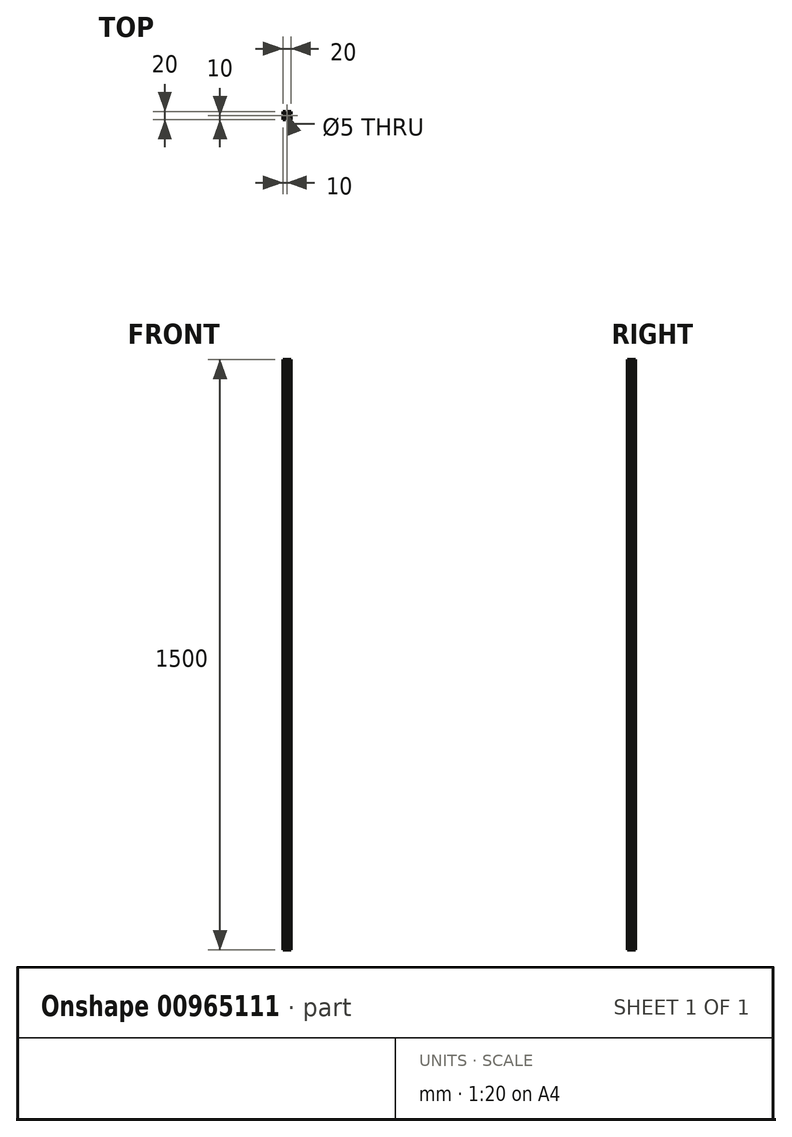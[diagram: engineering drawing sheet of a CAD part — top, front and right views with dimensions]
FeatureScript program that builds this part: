
annotation { "Feature Type Name" : "Feature", "Feature Type Description" : "" }
export const myFeature = defineFeature(function(context is Context, id is Id, definition is map)
    precondition{}
    {
        {
            var Q0;
            Q0=qCreatedBy(makeId("Top.planeOp"),FACE);
            var sketch = newSketch(context, id + "F0", { "sketchPlane" : qUnion([Q0])});
            skCircle(sketch, "E0", {"center": v(10, 10) * mm, "radius": 2.5 * mm});
            skLineSegment(sketch, "E1", {"start": v(0, 0) * mm, "end": v(10, 10) * mm, "construction": true});
            skLineSegment(sketch, "E2", {"start": v(1.4, 2.39) * mm, "end": v(1.4, 6.8) * mm});
            skLineSegment(sketch, "E3", {"start": v(1.4, 6.8) * mm, "end": v(0, 6.8) * mm});
            skLineSegment(sketch, "E4", {"start": v(0, 6.8) * mm, "end": v(0, 0) * mm});
            skLineSegment(sketch, "E5", {"start": v(7.49, 6.5) * mm, "end": v(2.39, 1.4) * mm});
            skLineSegment(sketch, "E6", {"start": v(2.39, 1.4) * mm, "end": v(6.8, 1.4) * mm});
            skLineSegment(sketch, "E7", {"start": v(6.8, 1.4) * mm, "end": v(6.8, 0) * mm});
            skLineSegment(sketch, "E8", {"start": v(6.8, 0) * mm, "end": v(0, 0) * mm});
            skLineSegment(sketch, "E9", {"start": v(10, 10) * mm, "end": v(20, 20) * mm, "construction": true});
            skLineSegment(sketch, "E10", {"start": v(10, 10) * mm, "end": v(0, 20) * mm, "construction": true});
            skLineSegment(sketch, "E11", {"start": v(10, 10) * mm, "end": v(20, 0) * mm, "construction": true});
            skLineSegment(sketch, "E12", {"start": v(1.4, 17.61) * mm, "end": v(6.5, 12.51) * mm});
            skLineSegment(sketch, "E13", {"start": v(1.4, 17.61) * mm, "end": v(1.4, 13.2) * mm});
            skLineSegment(sketch, "E14", {"start": v(1.4, 13.2) * mm, "end": v(0, 13.2) * mm});
            skLineSegment(sketch, "E15", {"start": v(0, 13.2) * mm, "end": v(0, 20) * mm});
            skLineSegment(sketch, "E16", {"start": v(7.49, 13.5) * mm, "end": v(2.39, 18.6) * mm});
            skLineSegment(sketch, "E17", {"start": v(2.39, 18.6) * mm, "end": v(6.8, 18.6) * mm});
            skLineSegment(sketch, "E18", {"start": v(6.8, 18.6) * mm, "end": v(6.8, 20) * mm});
            skLineSegment(sketch, "E19", {"start": v(6.8, 20) * mm, "end": v(0, 20) * mm});
            skLineSegment(sketch, "E20", {"start": v(12.51, 13.5) * mm, "end": v(17.61, 18.6) * mm});
            skLineSegment(sketch, "E21", {"start": v(17.61, 18.6) * mm, "end": v(13.2, 18.6) * mm});
            skLineSegment(sketch, "E22", {"start": v(13.2, 18.6) * mm, "end": v(13.2, 20) * mm});
            skLineSegment(sketch, "E23", {"start": v(13.2, 20) * mm, "end": v(20, 20) * mm});
            skLineSegment(sketch, "E24", {"start": v(13.5, 12.51) * mm, "end": v(18.6, 17.61) * mm});
            skLineSegment(sketch, "E25", {"start": v(18.6, 17.61) * mm, "end": v(18.6, 13.2) * mm});
            skLineSegment(sketch, "E26", {"start": v(18.6, 13.2) * mm, "end": v(20, 13.2) * mm});
            skLineSegment(sketch, "E27", {"start": v(20, 13.2) * mm, "end": v(20, 20) * mm});
            skLineSegment(sketch, "E28", {"start": v(18.6, 2.39) * mm, "end": v(18.6, 6.8) * mm});
            skLineSegment(sketch, "E29", {"start": v(18.6, 6.8) * mm, "end": v(20, 6.8) * mm});
            skLineSegment(sketch, "E30", {"start": v(20, 6.8) * mm, "end": v(20, 0) * mm});
            skLineSegment(sketch, "E31", {"start": v(12.51, 6.5) * mm, "end": v(17.61, 1.4) * mm});
            skLineSegment(sketch, "E32", {"start": v(17.61, 1.4) * mm, "end": v(13.2, 1.4) * mm});
            skLineSegment(sketch, "E33", {"start": v(13.2, 1.4) * mm, "end": v(13.2, 0) * mm});
            skLineSegment(sketch, "E34", {"start": v(13.2, 0) * mm, "end": v(20, 0) * mm});
            skLineSegment(sketch, "E35", {"start": v(12.51, 6.5) * mm, "end": v(7.49, 6.5) * mm});
            skLineSegment(sketch, "E36", {"start": v(7.49, 13.5) * mm, "end": v(12.51, 13.5) * mm});
            skLineSegment(sketch, "E37", {"start": v(10, 10) * mm, "end": v(10, 0) * mm, "construction": true});
            skLineSegment(sketch, "E38", {"start": v(10, 10) * mm, "end": v(18.77, 10) * mm, "construction": true});
            skLineSegment(sketch, "E39", {"start": v(10, 10) * mm, "end": v(10, 20.74) * mm, "construction": true});
            skLineSegment(sketch, "E40", {"start": v(10, 10) * mm, "end": v(0, 10) * mm, "construction": true});
            skLineSegment(sketch, "E41.bottom", {"start": v(0, 0) * mm, "end": v(20, 0) * mm, "construction": true});
            skLineSegment(sketch, "E41.top", {"start": v(0, 20) * mm, "end": v(20, 20) * mm, "construction": true});
            skLineSegment(sketch, "E41.left", {"start": v(0, 0) * mm, "end": v(0, 20) * mm, "construction": true});
            skLineSegment(sketch, "E41.right", {"start": v(20, 0) * mm, "end": v(20, 20) * mm, "construction": true});
            skLineSegment(sketch, "E42", {"start": v(18.6, 2.39) * mm, "end": v(13.5, 7.49) * mm});
            skLineSegment(sketch, "E43", {"start": v(13.5, 7.49) * mm, "end": v(13.5, 12.51) * mm});
            skLineSegment(sketch, "E44", {"start": v(1.4, 2.39) * mm, "end": v(6.5, 7.62) * mm});
            skLineSegment(sketch, "E45", {"start": v(6.5, 7.62) * mm, "end": v(6.5, 12.51) * mm});
            skSolve(sketch);
        }
        {
            var Q0;
            Q0=makeQuery(id+"F0.imprint","IMPRINT",FACE,{"disambiguationData":[TD([[makeQuery(id+"F0.imprint","IMPRINT",EDGE,{"derivedFrom":sQuery(id+"F0.wireOp",EDGE,"E0")}),-1.0]])]});
            extrude(context, id + "F1", {"entities" : qUnion([Q0]), "depth" : 1500 * mm, "offsetDistance" : 25 * mm});
        }
    });
